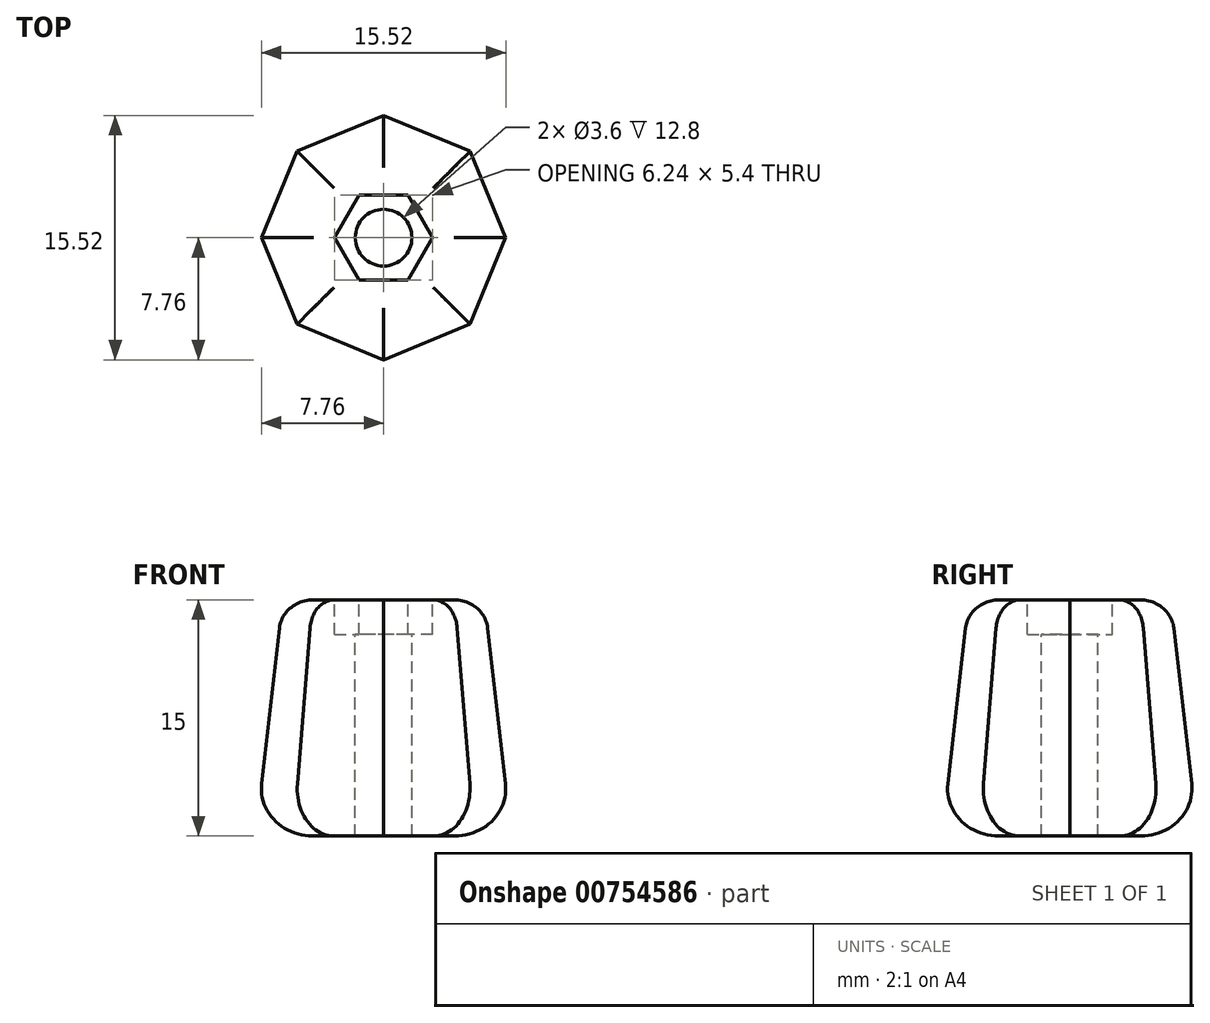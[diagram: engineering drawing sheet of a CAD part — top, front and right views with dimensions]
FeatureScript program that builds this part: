
annotation { "Feature Type Name" : "Feature", "Feature Type Description" : "" }
export const myFeature = defineFeature(function(context is Context, id is Id, definition is map)
    precondition{}
    {
        {
            var Q0;
            Q0=qCreatedBy(makeId("Top.planeOp"),FACE);
            var sketch = newSketch(context, id + "F0", { "sketchPlane" : qUnion([Q0])});
            skCircle(sketch, "E0.cCircle", {"center": v(0, 0) * mm, "radius": 7.5 * mm, "construction": true});
            skLineSegment(sketch, "E0.0", {"start": v(-8.12, 0) * mm, "end": v(-5.74, 5.74) * mm});
            skLineSegment(sketch, "E0.1", {"start": v(-5.74, 5.74) * mm, "end": v(0, 8.12) * mm});
            skLineSegment(sketch, "E0.2", {"start": v(0, 8.12) * mm, "end": v(5.74, 5.74) * mm});
            skLineSegment(sketch, "E0.3", {"start": v(5.74, 5.74) * mm, "end": v(8.12, 0) * mm});
            skLineSegment(sketch, "E0.4", {"start": v(8.12, 0) * mm, "end": v(5.74, -5.74) * mm});
            skLineSegment(sketch, "E0.5", {"start": v(5.74, -5.74) * mm, "end": v(0, -8.12) * mm});
            skLineSegment(sketch, "E0.6", {"start": v(0, -8.12) * mm, "end": v(-5.74, -5.74) * mm});
            skLineSegment(sketch, "E0.7", {"start": v(-5.74, -5.74) * mm, "end": v(-8.12, 0) * mm});
            skPoint(sketch, "E0.0.midPoint", {"position": v(-6.93, 2.87) * mm});
            skSolve(sketch);
        }
        {
            var Q0;
            Q0 = qSketchRegion(id + "F0", true);
            extrude(context, id + "F1", {"entities" : qUnion([Q0]), "depth" : 15 * mm, "offsetDistance" : 25 * mm, "hasDraft" : true, "draftAngle" : 6 * degree, "draftPullDirection" : true});
        }
        {
            var Q0;
            Q0=makeQuery(id+"F1.opExtrude","CAP_FACE",FACE,{"disambiguationData":[OSD([sQuery(id+"F0.wireOp",EDGE,"E0.0"),sQuery(id+"F0.wireOp",EDGE,"E0.1"),sQuery(id+"F0.wireOp",EDGE,"E0.2"),sQuery(id+"F0.wireOp",EDGE,"E0.3"),sQuery(id+"F0.wireOp",EDGE,"E0.4"),sQuery(id+"F0.wireOp",EDGE,"E0.5"),sQuery(id+"F0.wireOp",EDGE,"E0.6"),sQuery(id+"F0.wireOp",EDGE,"E0.7")])],"isStart":false});
            var sketch = newSketch(context, id + "F2", { "sketchPlane" : qUnion([Q0])});
            skCircle(sketch, "E1", {"center": v(0, 0) * mm, "radius": 1.8 * mm});
            skSolve(sketch);
        }
        {
            var Q0;
            Q0 = qSketchRegion(id + "F2", true);
            extrude(context, id + "F3", {"entities" : qUnion([Q0]), "operationType" : NewBodyOperationType.REMOVE, "endBound" : BoundingType.THROUGH_ALL, "oppositeDirection" : true, "depth" : 25 * mm, "offsetDistance" : 25 * mm});
        }
        {
            var Q0;
            Q0=makeQuery(id+"F1.opExtrude","CAP_FACE",FACE,{"disambiguationData":[OSD([sQuery(id+"F0.wireOp",EDGE,"E0.0"),sQuery(id+"F0.wireOp",EDGE,"E0.1"),sQuery(id+"F0.wireOp",EDGE,"E0.2"),sQuery(id+"F0.wireOp",EDGE,"E0.3"),sQuery(id+"F0.wireOp",EDGE,"E0.4"),sQuery(id+"F0.wireOp",EDGE,"E0.5"),sQuery(id+"F0.wireOp",EDGE,"E0.6"),sQuery(id+"F0.wireOp",EDGE,"E0.7")])],"isStart":false});
            var sketch = newSketch(context, id + "F4", { "sketchPlane" : qUnion([Q0])});
            skCircle(sketch, "E2.cCircle", {"center": v(0, 0) * mm, "radius": 2.7 * mm, "construction": true});
            skLineSegment(sketch, "E2.0", {"start": v(-3.12, 0) * mm, "end": v(-1.56, 2.7) * mm});
            skLineSegment(sketch, "E2.1", {"start": v(-1.56, 2.7) * mm, "end": v(1.56, 2.7) * mm});
            skLineSegment(sketch, "E2.2", {"start": v(1.56, 2.7) * mm, "end": v(3.12, 0) * mm});
            skLineSegment(sketch, "E2.3", {"start": v(3.12, 0) * mm, "end": v(1.56, -2.7) * mm});
            skLineSegment(sketch, "E2.4", {"start": v(1.56, -2.7) * mm, "end": v(-1.56, -2.7) * mm});
            skLineSegment(sketch, "E2.5", {"start": v(-1.56, -2.7) * mm, "end": v(-3.12, 0) * mm});
            skPoint(sketch, "E2.0.midPoint", {"position": v(-2.34, 1.35) * mm});
            skSolve(sketch);
        }
        {
            var Q0;
            Q0 = qSketchRegion(id + "F4", true);
            extrude(context, id + "F5", {"entities" : qUnion([Q0]), "operationType" : NewBodyOperationType.REMOVE, "oppositeDirection" : true, "depth" : 2.2 * mm, "offsetDistance" : 25 * mm});
        }
        {
            var Q0;
            Q0=makeQuery(id+"F1.opExtrude","CAP_EDGE",EDGE,{"disambiguationData":[OSD([sQuery(id+"F0.wireOp",EDGE,"E0.7")])],"isStart":false});
            var Q1;
            Q1=makeQuery(id+"F1.opExtrude","CAP_EDGE",EDGE,{"disambiguationData":[OSD([sQuery(id+"F0.wireOp",EDGE,"E0.6")])],"isStart":false});
            var Q2;
            Q2=makeQuery(id+"F1.opExtrude","CAP_EDGE",EDGE,{"disambiguationData":[OSD([sQuery(id+"F0.wireOp",EDGE,"E0.5")])],"isStart":false});
            var Q3;
            Q3=makeQuery(id+"F1.opExtrude","CAP_EDGE",EDGE,{"disambiguationData":[OSD([sQuery(id+"F0.wireOp",EDGE,"E0.4")])],"isStart":false});
            var Q4;
            Q4=makeQuery(id+"F1.opExtrude","CAP_EDGE",EDGE,{"disambiguationData":[OSD([sQuery(id+"F0.wireOp",EDGE,"E0.3")])],"isStart":false});
            var Q5;
            Q5=makeQuery(id+"F1.opExtrude","CAP_EDGE",EDGE,{"disambiguationData":[OSD([sQuery(id+"F0.wireOp",EDGE,"E0.2")])],"isStart":false});
            var Q6;
            Q6=makeQuery(id+"F1.opExtrude","CAP_EDGE",EDGE,{"disambiguationData":[OSD([sQuery(id+"F0.wireOp",EDGE,"E0.1")])],"isStart":false});
            var Q7;
            Q7=makeQuery(id+"F1.opExtrude","CAP_EDGE",EDGE,{"disambiguationData":[OSD([sQuery(id+"F0.wireOp",EDGE,"E0.0")])],"isStart":false});
            fillet(context, id + "F6", {"entities" : qUnion([Q0, Q1, Q2, Q3, Q4, Q5, Q6, Q7]), "radius" : 2 * mm, "tangentPropagation" : true, "allowEdgeOverflow" : false});
        }
        {
            var Q0;
            Q0=makeQuery(id+"F1.opExtrude","CAP_EDGE",EDGE,{"disambiguationData":[OSD([sQuery(id+"F0.wireOp",EDGE,"E0.6")])],"isStart":true});
            var Q1;
            Q1=makeQuery(id+"F1.opExtrude","CAP_EDGE",EDGE,{"disambiguationData":[OSD([sQuery(id+"F0.wireOp",EDGE,"E0.7")])],"isStart":true});
            var Q2;
            Q2=makeQuery(id+"F1.opExtrude","CAP_EDGE",EDGE,{"disambiguationData":[OSD([sQuery(id+"F0.wireOp",EDGE,"E0.5")])],"isStart":true});
            var Q3;
            Q3=makeQuery(id+"F1.opExtrude","CAP_EDGE",EDGE,{"disambiguationData":[OSD([sQuery(id+"F0.wireOp",EDGE,"E0.4")])],"isStart":true});
            var Q4;
            Q4=makeQuery(id+"F1.opExtrude","CAP_EDGE",EDGE,{"disambiguationData":[OSD([sQuery(id+"F0.wireOp",EDGE,"E0.3")])],"isStart":true});
            var Q5;
            Q5=makeQuery(id+"F1.opExtrude","CAP_EDGE",EDGE,{"disambiguationData":[OSD([sQuery(id+"F0.wireOp",EDGE,"E0.2")])],"isStart":true});
            var Q6;
            Q6=makeQuery(id+"F1.opExtrude","CAP_EDGE",EDGE,{"disambiguationData":[OSD([sQuery(id+"F0.wireOp",EDGE,"E0.1")])],"isStart":true});
            var Q7;
            Q7=makeQuery(id+"F1.opExtrude","CAP_EDGE",EDGE,{"disambiguationData":[OSD([sQuery(id+"F0.wireOp",EDGE,"E0.0")])],"isStart":true});
            fillet(context, id + "F7", {"entities" : qUnion([Q0, Q1, Q2, Q3, Q4, Q5, Q6, Q7]), "radius" : 3 * mm, "tangentPropagation" : true, "allowEdgeOverflow" : false});
        }
    });
